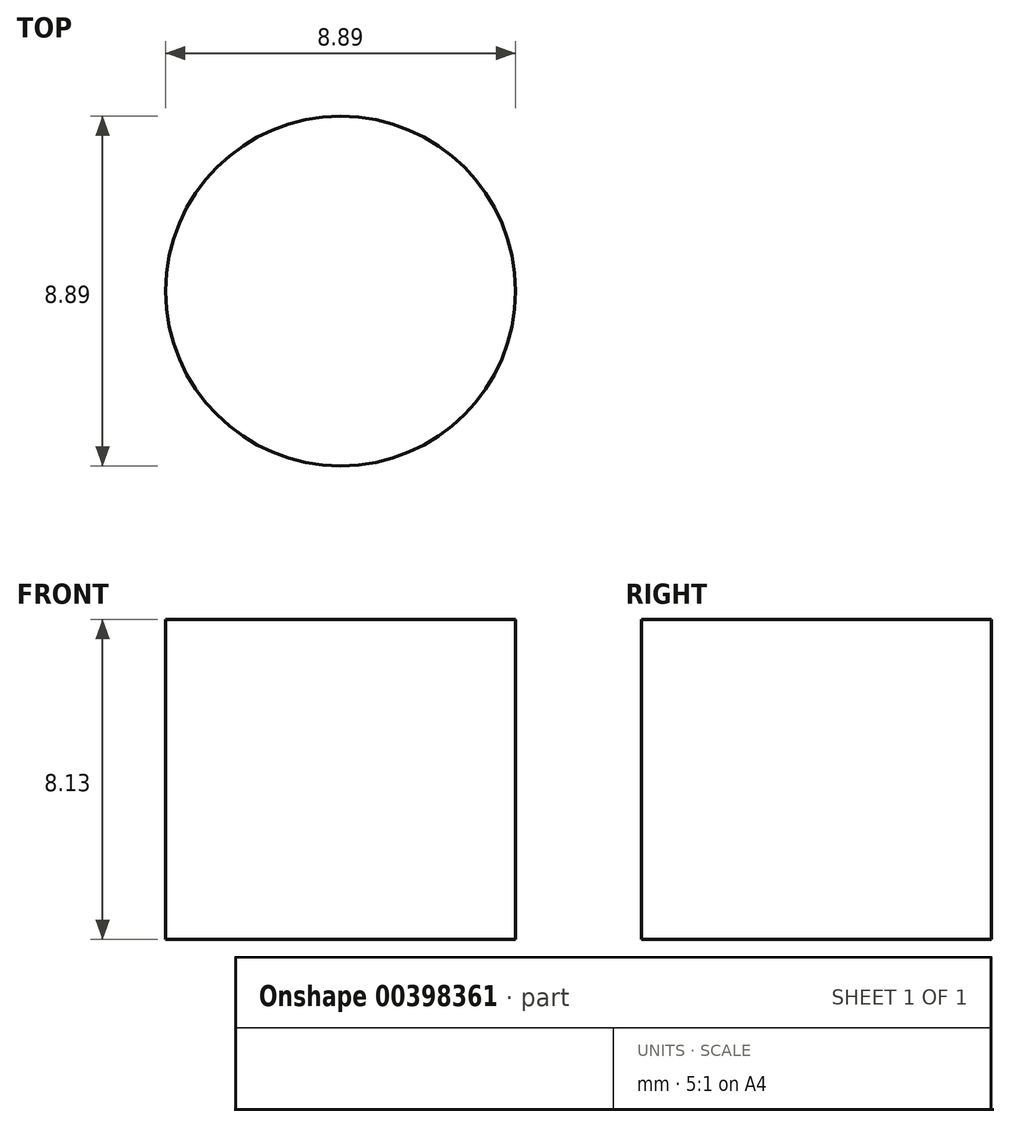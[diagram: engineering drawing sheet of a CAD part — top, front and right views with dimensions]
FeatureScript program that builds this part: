
annotation { "Feature Type Name" : "Feature", "Feature Type Description" : "" }
export const myFeature = defineFeature(function(context is Context, id is Id, definition is map)
    precondition{}
    {
        {
            var Q0;
            Q0=qCreatedBy(makeId("Top.planeOp"),FACE);
            var sketch = newSketch(context, id + "F0", { "sketchPlane" : qUnion([Q0])});
            skCircle(sketch, "E0", {"center": v(-61.85, -3.99) * mm, "radius": 4.44 * mm});
            skSolve(sketch);
        }
        {
            var Q0;
            Q0=makeQuery(id+"F0.imprint","IMPRINT",FACE,{"disambiguationData":[TD([[makeQuery(id+"F0.imprint","IMPRINT",EDGE,{"derivedFrom":sQuery(id+"F0.wireOp",EDGE,"E0")}),1.0]])]});
            extrude(context, id + "F1", {"entities" : qUnion([Q0]), "depth" : 8.13 * mm});
        }
    });
